# Revit family: Фильтр
name_source: partatom
category: Арматура трубопроводов
revit_build: Autodesk Revit 2017 (Build: 20171027_0315(x64)
units: mm (PartAtom-declared; Revit-internal decimal feet)

## family parameters
Всегда вертикально = Да
На основе рабочей плоскости = Нет
Общий = Нет
При загрузке вырезать с полостями = Нет
Размер круглого соединителя = Использовать радиус
Тип детали = Вставляется

## types (11) — shared parameters
ADSK_Единица измерения = шт
ADSK_Завод-изготовитель = Itap
ADSK_Наименование = Фильтр механической очистки
URL = http://www.itap.it
Группа модели = Фильтр механической очистки
Изготовитель = Itap
Материал фитинга = Фильтр_Латунь
Разработчик = ООО ПРОРУБИМ
Разработчик (телефон) = +7(495)649-85-43
Разработчик модели (URL) = http://prorubim.com
zero-valued in all types: ADSK_Масса

## per-type parameters (varying)
| type | A | ADSK_Код изделия | B | B1 | B2 | C | DN | DN+t | DN+t/2 | R | S | l1 | l2 | Переключатель УГО |
| DN100 | 219 мм |  | 162 мм | 41 мм | 14 мм | 225 мм | 100 мм | 104 мм | 52 мм | 50 мм | 177 мм | 43 мм | 55 мм | Нет |
| DN80 | 169 мм |  | 120 мм | 30 мм | 10 мм | 169 мм | 80 мм | 84 мм | 42 мм | 40 мм | 142 мм | 33 мм | 42 мм | Нет |
| DN65 | 150 мм |  | 105 мм | 26 мм | 9 мм | 148 мм | 65 мм | 69 мм | 35 мм | 33 мм | 115 мм | 30 мм | 38 мм | Нет |
| DN50 | 126 мм |  | 89 мм | 22 мм | 7 мм | 122 мм | 50 мм | 54 мм | 27 мм | 25 мм | 88 мм | 25 мм | 32 мм | Нет |
| DN40 | 106 мм | 27522 | 73 мм | 18 мм | 6 мм | 100 мм | 40 мм | 44 мм | 22 мм | 20 мм | 71 мм | 21 мм | 27 мм | Нет |
| DN32 | 96 мм | 26131 | 64 мм | 16 мм | 5 мм | 88 мм | 32 мм | 36 мм | 18 мм | 16 мм | 57 мм | 19 мм | 24 мм | Нет |
| DN25 | 87 мм | 12164 | 56 мм | 14 мм | 5 мм | 76 мм | 25 мм | 29 мм | 15 мм | 13 мм | 44 мм | 17 мм | 22 мм | Нет |
| DN20 | 70 мм | 27521 | 48 мм | 12 мм | 4 мм | 65 мм | 20 мм | 24 мм | 12 мм | 10 мм | 35 мм | 14 мм | 18 мм | Нет |
| DN15 | 58 мм |  | 40 мм | 10 мм | 3 мм | 53 мм | 15 мм | 19 мм | 10 мм | 8 мм | 27 мм | 11 мм | 15 мм | Да |
| DN10 | 55 мм |  | 40 мм | 10 мм | 3 мм | 51 мм | 10 мм | 14 мм | 7 мм | 5 мм | 18 мм | 11 мм | 14 мм | Нет |
| DN8 | 55 мм |  | 40 мм | 10 мм | 3 мм | 50 мм | 8 мм | 12 мм | 6 мм | 4 мм | 14 мм | 11 мм | 14 мм | Нет |

note: column(s) folded — value = type name in every type: ADSK_Обозначение
